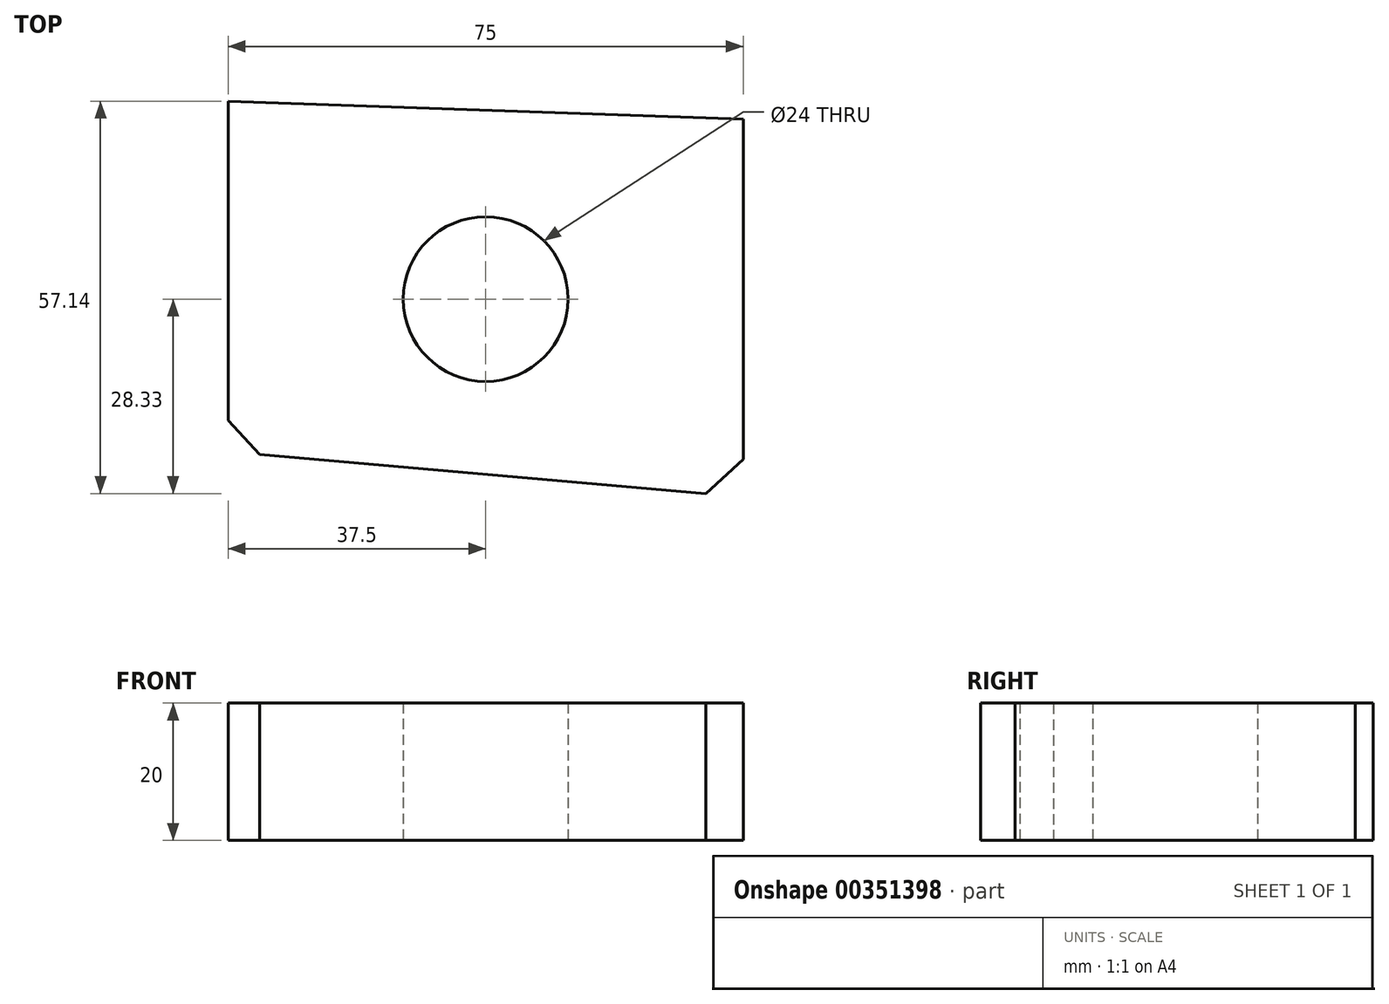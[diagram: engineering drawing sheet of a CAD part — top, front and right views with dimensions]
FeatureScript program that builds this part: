
annotation { "Feature Type Name" : "Feature", "Feature Type Description" : "" }
export const myFeature = defineFeature(function(context is Context, id is Id, definition is map)
    precondition{}
    {
        {
            var Q0;
            Q0=qCreatedBy(makeId("Top.planeOp"),FACE);
            var sketch = newSketch(context, id + "F0", { "sketchPlane" : qUnion([Q0])});
            skLineSegment(sketch, "E0.bottom", {"start": v(37.5, -28.8) * mm, "end": v(-37.5, -22.25) * mm});
            skLineSegment(sketch, "E0.top", {"start": v(37.5, 26.2) * mm, "end": v(-37.5, 28.8) * mm});
            skLineSegment(sketch, "E0.left", {"start": v(37.5, -28.8) * mm, "end": v(37.5, 26.2) * mm});
            skLineSegment(sketch, "E0.right", {"start": v(-37.5, -22.25) * mm, "end": v(-37.5, 28.8) * mm});
            skPoint(sketch, "E1.visualSharp", {"position": v(-37.5, -22.25) * mm});
            skPoint(sketch, "E2.visualSharp", {"position": v(37.5, -28.8) * mm});
            skSolve(sketch);
        }
        {
            var Q0;
            Q0=makeQuery(id+"F0.imprint","IMPRINT",FACE,{"disambiguationData":[TD([[makeQuery(id+"F0.imprint","IMPRINT",EDGE,{"derivedFrom":sQuery(id+"F0.wireOp",EDGE,"E0.bottom")}),-1.0]])]});
            extrude(context, id + "F1", {"entities" : qUnion([Q0]), "depth" : 20 * mm});
        }
        {
            var Q0;
            Q0=makeQuery(id+"F1.opExtrude","SWEPT_EDGE",EDGE,{"disambiguationData":[OSD([sQuery(id+"F0.wireOp",EDGE,"E0.bottom"),sQuery(id+"F0.wireOp",EDGE,"E0.left")])]});
            var Q1;
            Q1=makeQuery(id+"F1.opExtrude","SWEPT_EDGE",EDGE,{"disambiguationData":[OSD([sQuery(id+"F0.wireOp",EDGE,"E0.bottom"),sQuery(id+"F0.wireOp",EDGE,"E0.right")])]});
            chamfer(context, id + "F2", {"entities" : qUnion([Q0, Q1]), "width" : 5 * mm, "tangentPropagation" : true});
        }
        {
            var Q0;
            Q0=makeQuery(id+"F1.opExtrude","CAP_FACE",FACE,{"disambiguationData":[OSD([sQuery(id+"F0.wireOp",EDGE,"E0.bottom"),sQuery(id+"F0.wireOp",EDGE,"E0.top"),sQuery(id+"F0.wireOp",EDGE,"E0.left"),sQuery(id+"F0.wireOp",EDGE,"E0.right")])],"isStart":true});
            var sketch = newSketch(context, id + "F3", { "sketchPlane" : qUnion([Q0])});
            skCircle(sketch, "E3", {"center": v(0, 0) * mm, "radius": 12 * mm});
            skSolve(sketch);
        }
        {
            var Q0;
            Q0=makeQuery(id+"F3.imprint","IMPRINT",FACE,{"disambiguationData":[TD([[makeQuery(id+"F3.imprint","IMPRINT",EDGE,{"derivedFrom":sQuery(id+"F3.wireOp",EDGE,"E3")}),1.0]])]});
            var Q1;
            Q1=sQuery(id+"F3.wireOp",EDGE,"E3");
            extrude(context, id + "F4", {"entities" : qUnion([Q0]), "operationType" : NewBodyOperationType.REMOVE, "surfaceEntities" : qUnion([Q1]), "endBound" : BoundingType.THROUGH_ALL, "oppositeDirection" : true, "depth" : 15 * mm});
        }
    });
